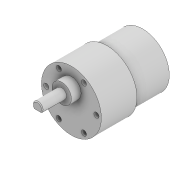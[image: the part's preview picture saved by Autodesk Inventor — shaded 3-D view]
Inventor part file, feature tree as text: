
AUTODESK INVENTOR PART (.ipt)
format: ipt  version: 2022 (Build 260153000, 153)  size: 142,336 bytes
history: native  units: mm
features: sketch x6, extrude x5, projected_geometry x2, chamfer x1, hole x1
ambient origin geometry x8: Origin, YZ Plane, XZ Plane, XY Plane, X Axis, Y Axis, Z Axis, Center Point
bodies: Solid1 (feature_tree)
feature tree (15):
  extrude  "Extrusion1"  Depth=22.0mm TaperAngle=0.0deg
  extrude  "Extrusion2"  Depth=22.0mm TaperAngle=0.0deg
  extrude  "Extrusion3"  Depth=7.0mm
  extrude  "Extrusion4"  Depth=6.0mm
  extrude  "Extrusion5"  Depth=3.0mm
  chamfer  "Chamfer1"  Distance=12.0mm
  hole  "Hole1"  [1 undecoded]
  sketch  "Sketch1"  dims[d0=33.0mm d1=22.0mm d2=0.0mm]
  sketch  "Sketch2"  dims[d4=37.0mm d5=22.0mm d6=0.0mm]
  sketch  "Sketch3"  dims[d7=12.0mm d8=7.0mm]
  sketch  "Sketch4"  dims[d9=6.0mm d10=0.0mm d11=6.0mm]
  sketch  "Sketch5"  dims[d12=3.0mm d13=0.0mm d14=5.2mm d15=12.0mm d16=0.0mm]
  sketch  "Sketch6"  dims[d17=0.5mm d18=2.0mm d19=45.0deg d20=31.0mm d21=30.0mm d23=120.0deg d25=3.2mm d26=6.0mm d27=4.0mm d28=2.0mm d29=90.0deg d30=3.5mm d31=20.594885mm]
  projected_geometry  "Project Cut Edges1"
  projected_geometry  "Project Cut Edges2"
note: 1 required parameter value undecoded (feature->parameter linkage not recoverable at this tier; creation-order binding heuristic only, values carry confidence <= 0.55)
